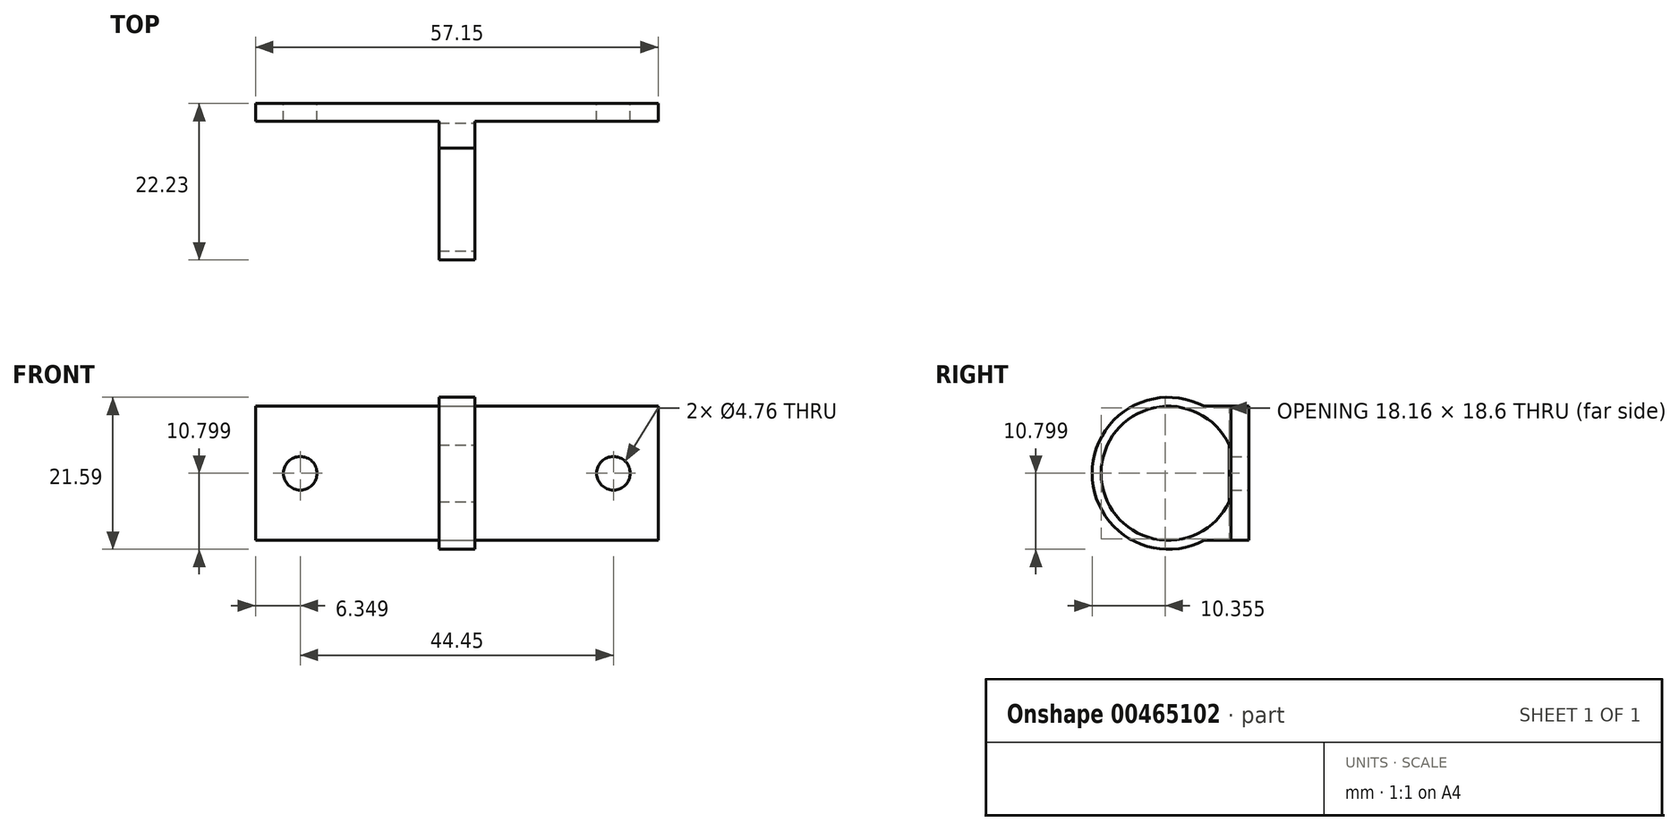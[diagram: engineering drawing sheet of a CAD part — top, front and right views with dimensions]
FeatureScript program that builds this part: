
annotation { "Feature Type Name" : "Feature", "Feature Type Description" : "" }
export const myFeature = defineFeature(function(context is Context, id is Id, definition is map)
    precondition{}
    {
        {
            var Q0;
            Q0=qCreatedBy(makeId("Front.planeOp"),FACE);
            var sketch = newSketch(context, id + "F0", { "sketchPlane" : qUnion([Q0])});
            skLineSegment(sketch, "E0.bottom", {"start": v(-25.56, 32.65) * mm, "end": v(31.59, 32.65) * mm});
            skLineSegment(sketch, "E0.top", {"start": v(-25.56, 13.6) * mm, "end": v(31.59, 13.6) * mm});
            skLineSegment(sketch, "E0.left", {"start": v(-25.56, 32.65) * mm, "end": v(-25.56, 13.6) * mm});
            skLineSegment(sketch, "E0.right", {"start": v(31.59, 32.65) * mm, "end": v(31.59, 13.6) * mm});
            skCircle(sketch, "E1", {"center": v(-19.21, 23.13) * mm, "radius": 2.38 * mm});
            skCircle(sketch, "E2", {"center": v(25.24, 23.13) * mm, "radius": 2.38 * mm});
            skSolve(sketch);
        }
        {
            var Q0;
            Q0 = qSketchRegion(id + "F0", true);
            extrude(context, id + "F1", {"entities" : qUnion([Q0]), "depth" : 2.54 * mm});
        }
        {
            var Q0;
            Q0=makeQuery(id+"F1.opExtrude","CAP_FACE",FACE,{"disambiguationData":[OSD([sQuery(id+"F0.wireOp",EDGE,"E0.bottom"),sQuery(id+"F0.wireOp",EDGE,"E0.top"),sQuery(id+"F0.wireOp",EDGE,"E0.left"),sQuery(id+"F0.wireOp",EDGE,"E0.right"),sQuery(id+"F0.wireOp",EDGE,"E1"),sQuery(id+"F0.wireOp",EDGE,"E2")])],"isStart":false});
            var sketch = newSketch(context, id + "F2", { "sketchPlane" : qUnion([Q0])});
            skLineSegment(sketch, "E3.bottom", {"start": v(5.55, 16.14) * mm, "end": v(0.47, 16.14) * mm});
            skLineSegment(sketch, "E3.top", {"start": v(5.55, 30.11) * mm, "end": v(0.47, 30.11) * mm});
            skLineSegment(sketch, "E3.left", {"start": v(5.55, 16.14) * mm, "end": v(5.55, 30.11) * mm});
            skLineSegment(sketch, "E3.right", {"start": v(0.47, 16.14) * mm, "end": v(0.47, 30.11) * mm});
            skPoint(sketch, "E3.middle", {"position": v(3.01, 23.13) * mm});
            skSolve(sketch);
        }
        {
            var Q0;
            Q0 = qSketchRegion(id + "F2", true);
            extrude(context, id + "F3", {"entities" : qUnion([Q0]), "operationType" : NewBodyOperationType.ADD, "depth" : 0.25 * mm});
        }
        {
            var Q0;
            Q0=makeQuery(id+"F3.opExtrude","SWEPT_FACE",FACE,{"disambiguationData":[OSD([sQuery(id+"F2.wireOp",EDGE,"E3.left")])]});
            var sketch = newSketch(context, id + "F4", { "sketchPlane" : qUnion([Q0])});
            skArc(sketch, "E4", {"start": v(-2.54, 26.55) * mm, "mid": v(-20.96, 23.13) * mm, "end": v(-2.54, 19.71) * mm});
            skArc(sketch, "E5.0", {"start": v(-6.35, 32.65) * mm, "mid": v(-22.23, 23.13) * mm, "end": v(-6.35, 13.6) * mm});
            skLineSegment(sketch, "E6.bottom", {"start": v(-2.54, 13.6) * mm, "end": v(-6.35, 13.6) * mm});
            skLineSegment(sketch, "E6.top", {"start": v(-2.54, 32.65) * mm, "end": v(-6.35, 32.65) * mm});
            skLineSegment(sketch, "E6.left", {"start": v(-2.54, 13.6) * mm, "end": v(-2.54, 32.65) * mm});
            skPoint(sketch, "E7.0.3.end.orphan", {"position": v(0, 13.6) * mm});
            skPoint(sketch, "E7.0.1.end.orphan", {"position": v(-2.54, 32.65) * mm});
            skPoint(sketch, "E7.0.1.start.orphan", {"position": v(0, 32.65) * mm});
            skLineSegment(sketch, "E8", {"start": v(-2.8, 19.11) * mm, "end": v(-2.8, 27.14) * mm});
            skSolve(sketch);
        }
        {
            var Q0;
            Q0 = qSketchRegion(id + "F4", true);
            extrude(context, id + "F5", {"entities" : qUnion([Q0]), "operationType" : NewBodyOperationType.ADD, "oppositeDirection" : true, "depth" : 5.08 * mm});
        }
    });
